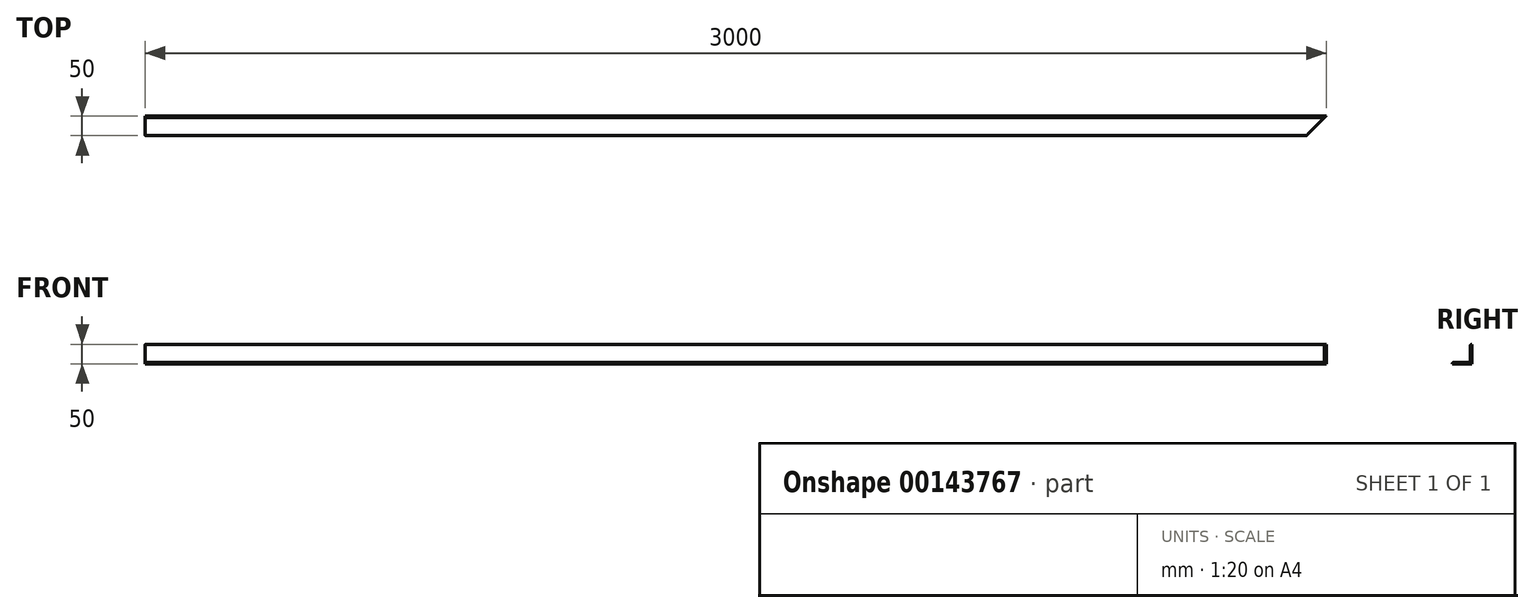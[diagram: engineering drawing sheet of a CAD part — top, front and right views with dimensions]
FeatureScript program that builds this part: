
annotation { "Feature Type Name" : "Feature", "Feature Type Description" : "" }
export const myFeature = defineFeature(function(context is Context, id is Id, definition is map)
    precondition{}
    {
        {
            var Q0;
            Q0=qCreatedBy(makeId("Right.planeOp"),FACE);
            var sketch = newSketch(context, id + "F0", { "sketchPlane" : qUnion([Q0])});
            skLineSegment(sketch, "E0", {"start": v(0, 50) * mm, "end": v(0, 0) * mm});
            skLineSegment(sketch, "E1", {"start": v(0, 0) * mm, "end": v(-50, 0) * mm});
            skLineSegment(sketch, "E2", {"start": v(0, 50) * mm, "end": v(0, 50) * mm});
            skLineSegment(sketch, "E3", {"start": v(-4, 46) * mm, "end": v(-4, 8) * mm});
            skLineSegment(sketch, "E4", {"start": v(-8, 4) * mm, "end": v(-46, 4) * mm});
            skLineSegment(sketch, "E5", {"start": v(-50, 0) * mm, "end": v(-50, 0) * mm});
            skPoint(sketch, "E6.visualSharp", {"position": v(-4, 50) * mm});
            skArc(sketch, "E6.filletArc", {"start": v(0, 50) * mm, "mid": v(-2.83, 48.83) * mm, "end": v(-4, 46) * mm});
            skPoint(sketch, "E7.visualSharp", {"position": v(-50, 4) * mm});
            skArc(sketch, "E7.filletArc", {"start": v(-46, 4) * mm, "mid": v(-48.83, 2.83) * mm, "end": v(-50, 0) * mm});
            skPoint(sketch, "E8.visualSharp", {"position": v(-4, 4) * mm});
            skArc(sketch, "E8.filletArc", {"start": v(-8, 4) * mm, "mid": v(-5.17, 5.17) * mm, "end": v(-4, 8) * mm});
            skSolve(sketch);
        }
        {
            var Q0;
            Q0=makeQuery(id+"F0.imprint","IMPRINT",FACE,{"disambiguationData":[TD([[makeQuery(id+"F0.imprint","IMPRINT",EDGE,{"derivedFrom":sQuery(id+"F0.wireOp",EDGE,"E0")}),-1.0]])]});
            extrude(context, id + "F1", {"entities" : qUnion([Q0]), "endBound" : BoundingType.SYMMETRIC, "depth" : 3000 * mm});
        }
        {
            var Q0;
            Q0=makeQuery(id+"F1.opExtrude","SWEPT_FACE",FACE,{"disambiguationData":[OSD([sQuery(id+"F0.wireOp",EDGE,"E1")])]});
            var sketch = newSketch(context, id + "F2", { "sketchPlane" : qUnion([Q0])});
            skLineSegment(sketch, "E9", {"start": v(1500, 0) * mm, "end": v(1500, 50) * mm});
            skLineSegment(sketch, "E10", {"start": v(1500, 50) * mm, "end": v(1450, 50) * mm});
            skLineSegment(sketch, "E11", {"start": v(1450, 50) * mm, "end": v(1500, 0) * mm});
            skSolve(sketch);
        }
        {
            var Q0;
            Q0 = qSketchRegion(id + "F2", true);
            extrude(context, id + "F3", {"entities" : qUnion([Q0]), "operationType" : NewBodyOperationType.REMOVE, "endBound" : BoundingType.THROUGH_ALL, "oppositeDirection" : true, "depth" : 25.4 * mm});
        }
    });
